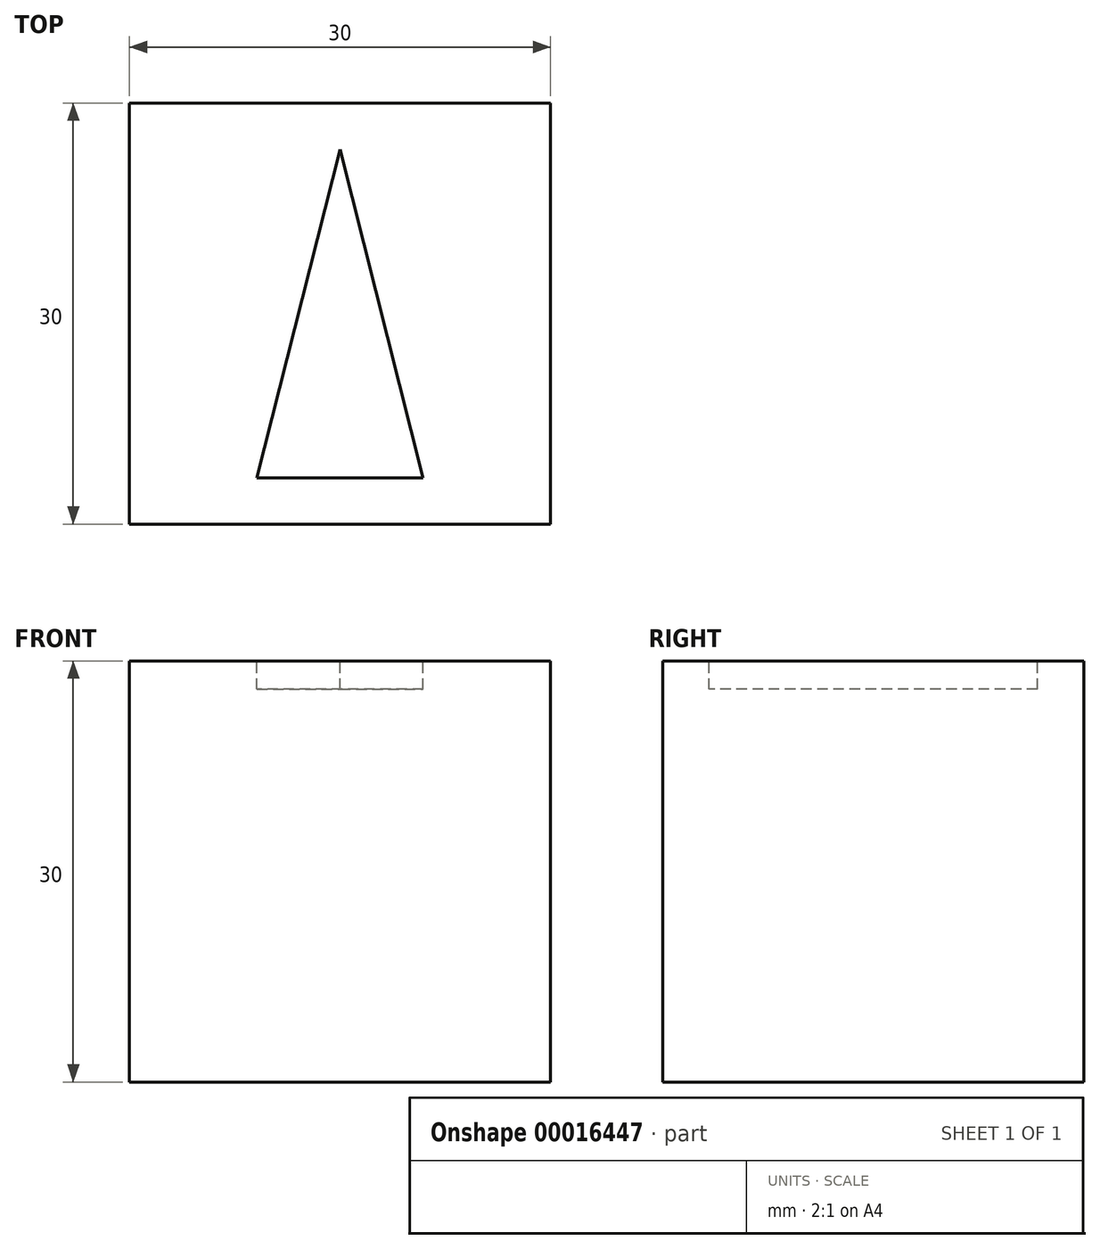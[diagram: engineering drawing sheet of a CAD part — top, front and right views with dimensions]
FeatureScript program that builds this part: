
annotation { "Feature Type Name" : "Feature", "Feature Type Description" : "" }
export const myFeature = defineFeature(function(context is Context, id is Id, definition is map)
    precondition{}
    {
        {
            var Q0;
            Q0=qCreatedBy(makeId("Top.planeOp"),FACE);
            var sketch = newSketch(context, id + "F0", { "sketchPlane" : qUnion([Q0])});
            skLineSegment(sketch, "E0.bottom", {"start": v(15, -15) * mm, "end": v(-15, -15) * mm});
            skLineSegment(sketch, "E0.top", {"start": v(15, 15) * mm, "end": v(-15, 15) * mm});
            skLineSegment(sketch, "E0.left", {"start": v(15, -15) * mm, "end": v(15, 15) * mm});
            skLineSegment(sketch, "E0.right", {"start": v(-15, -15) * mm, "end": v(-15, 15) * mm});
            skPoint(sketch, "E0.middle", {"position": v(0, 0) * mm});
            skSolve(sketch);
        }
        {
            var Q0;
            Q0=makeQuery(id+"F0.imprint","IMPRINT",FACE,{"disambiguationData":[TD([[makeQuery(id+"F0.imprint","IMPRINT",EDGE,{"derivedFrom":sQuery(id+"F0.wireOp",EDGE,"E0.bottom")}),-1.0]])]});
            extrude(context, id + "F1", {"entities" : qUnion([Q0]), "depth" : 30 * mm});
        }
        {
            var Q0;
            Q0=makeQuery(id+"F1.opExtrude","CAP_FACE",FACE,{"disambiguationData":[OSD([sQuery(id+"F0.wireOp",EDGE,"E0.bottom"),sQuery(id+"F0.wireOp",EDGE,"E0.top"),sQuery(id+"F0.wireOp",EDGE,"E0.left"),sQuery(id+"F0.wireOp",EDGE,"E0.right")])],"isStart":false});
            var sketch = newSketch(context, id + "F2", { "sketchPlane" : qUnion([Q0])});
            skLineSegment(sketch, "E1.bottom", {"start": v(5.92, -11.7) * mm, "end": v(-5.92, -11.7) * mm});
            skPoint(sketch, "E1.middle", {"position": v(0, 0) * mm});
            skLineSegment(sketch, "E2", {"start": v(-5.92, -11.7) * mm, "end": v(0, 11.7) * mm});
            skLineSegment(sketch, "E3", {"start": v(0, 11.7) * mm, "end": v(5.92, -11.7) * mm});
            skSolve(sketch);
        }
        {
            var Q0;
            Q0=makeQuery(id+"F2.imprint","IMPRINT",FACE,{"disambiguationData":[TD([[makeQuery(id+"F2.imprint","IMPRINT",EDGE,{"derivedFrom":sQuery(id+"F2.wireOp",EDGE,"E1.bottom")}),-1.0]])]});
            extrude(context, id + "F3", {"entities" : qUnion([Q0]), "operationType" : NewBodyOperationType.REMOVE, "oppositeDirection" : true, "depth" : 2 * mm});
        }
    });
